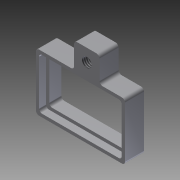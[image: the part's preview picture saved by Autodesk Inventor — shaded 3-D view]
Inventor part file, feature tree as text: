
AUTODESK INVENTOR PART (.ipt)
format: ipt  version: 2011 (Build 150239000, 239)  size: 160,768 bytes
history: native  units: in
note: dims shown in document units (in); Inventor stores cm internally (conversion verified against a paired STEP export)
features: sketch x6, extrude x5, hole x1, thread x1, fillet x1
ambient origin geometry x8: Origin, YZ Plane, XZ Plane, XY Plane, X Axis, Y Axis, Z Axis, Center Point
bodies: Solid1 (feature_tree)
feature tree (14):
  extrude  "Extrusion1"  Depth=0.3543in
  extrude  "Extrusion2"  Depth=0.4724in
  extrude  "Extrusion3"  Depth=0.1181in TaperAngle=0.0deg
  extrude  "Extrusion4"  Depth=0.2362in
  hole  "Hole1"  [1 undecoded]
  thread  "Thread1"  [1 undecoded]
  extrude  "Extrusion5"  Depth=1.0in TaperAngle=0.0deg
  fillet  "Fillet1"  Radius=0.0787in
  sketch  "Sketch1"  dims[d0=0.5512in d1=0.3543in]
  sketch  "Sketch2"  dims[d2=0.1181in d3=0.0in d4=0.4724in]
  sketch  "Sketch3"  dims[d5=0.2756in d6=0.1181in d7=0.0in]
  sketch  "Sketch5"  dims[d13=0.1575in d14=0.2362in]
  sketch  "Sketch6"  dims[d15=0.1575in d16=0.0in d17=0.0197in d18=0.0433in d19=0.0in]
  sketch  "Sketch7"  dims[d20=0.06in d21=0.75in d22=0.375in d23=0.25in d24=0.5635in d25=0.07in d26=0.8108in d27=1.0in d28=0.0in d29=0.0787in d30=0.0394in d31=0.2756in d32=0.0394in d33=0.0in d34=0.0197in]
note: 2 required parameter values undecoded (feature->parameter linkage not recoverable at this tier; creation-order binding heuristic only, values carry confidence <= 0.55)
